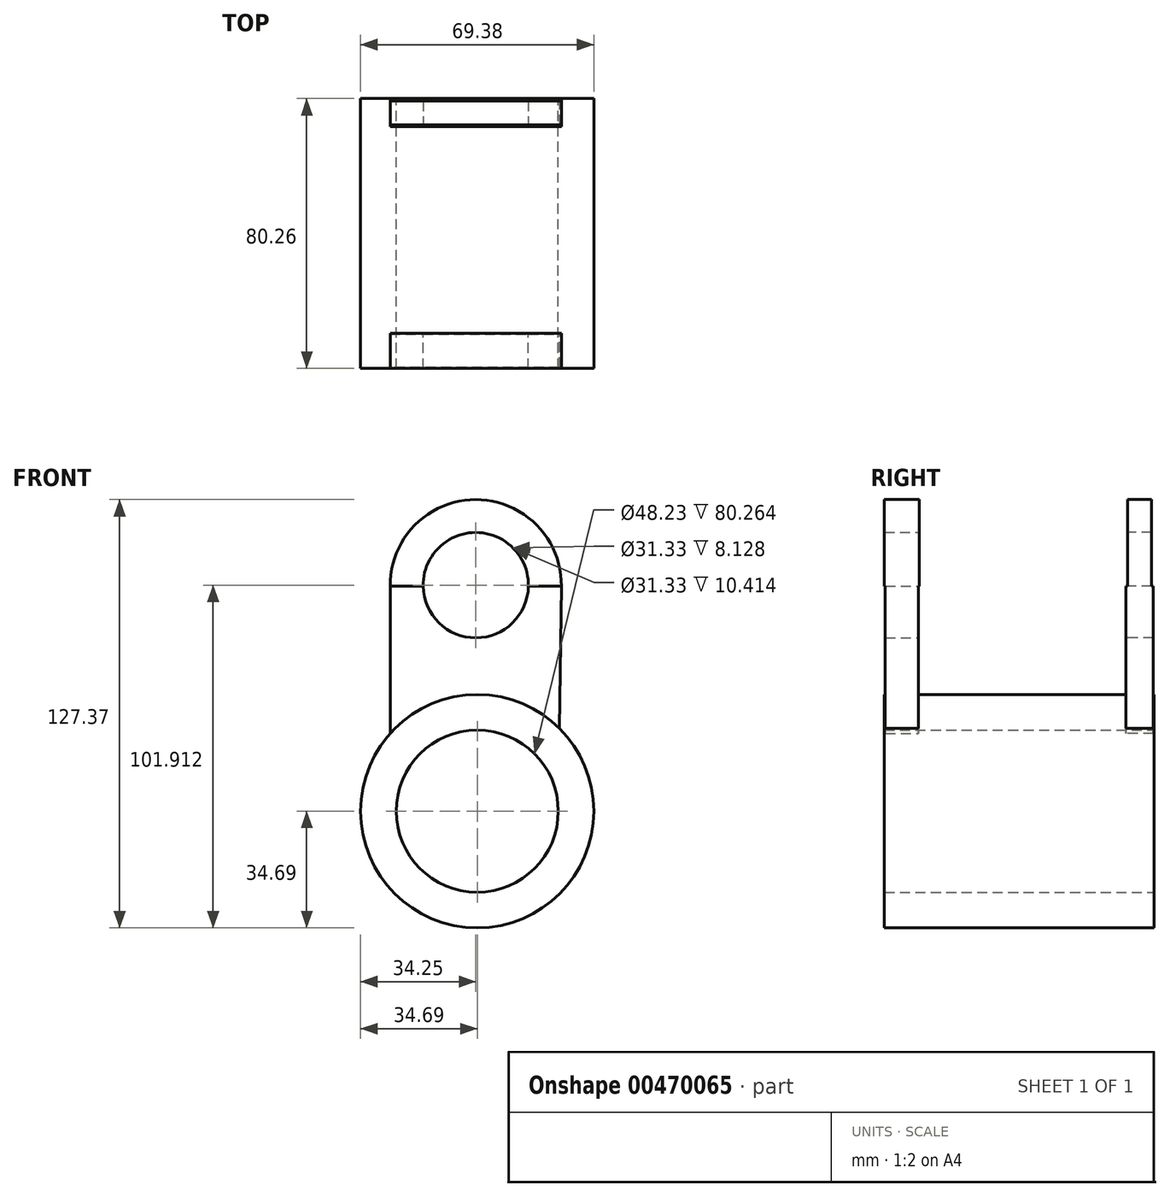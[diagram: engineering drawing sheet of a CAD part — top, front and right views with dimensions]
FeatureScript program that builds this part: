
annotation { "Feature Type Name" : "Feature", "Feature Type Description" : "" }
export const myFeature = defineFeature(function(context is Context, id is Id, definition is map)
    precondition{}
    {
        {
            var Q0;
            Q0=qCreatedBy(makeId("Front.planeOp"),FACE);
            var sketch = newSketch(context, id + "F0", { "sketchPlane" : qUnion([Q0])});
            skCircle(sketch, "E0", {"center": v(0, 0) * mm, "radius": 24.11 * mm});
            skCircle(sketch, "E1", {"center": v(0, 0) * mm, "radius": 34.69 * mm});
            skLineSegment(sketch, "E2", {"start": v(-25.9, 23.08) * mm, "end": v(-25.9, 66.88) * mm});
            skLineSegment(sketch, "E3", {"start": v(-25.9, 66.88) * mm, "end": v(25.02, 66.88) * mm});
            skLineSegment(sketch, "E4", {"start": v(25.02, 66.88) * mm, "end": v(24.45, 24.61) * mm});
            skArc(sketch, "E5", {"start": v(25.02, 66.88) * mm, "mid": v(-0.44, 92.68) * mm, "end": v(-25.9, 66.88) * mm});
            skCircle(sketch, "E6", {"center": v(-0.44, 67.22) * mm, "radius": 15.66 * mm});
            skSolve(sketch);
        }
        {
            var Q0;
            Q0=makeQuery(id+"F0.imprint","IMPRINT",FACE,{"disambiguationData":[TD([[makeQuery(id+"F0.imprint","IMPRINT",EDGE,{"derivedFrom":sQuery(id+"F0.wireOp",EDGE,"E0")}),-1.0]])]});
            extrude(context, id + "F1", {"entities" : qUnion([Q0]), "endBound" : BoundingType.SYMMETRIC, "depth" : 80.26 * mm});
        }
        {
            var Q0;
            {var subQ0=sQuery(id+"F0.wireOp",EDGE,"E2");Q0=makeQuery(id+"F0.imprint","IMPRINT",FACE,{"disambiguationData":[TD([[makeQuery(id+"F0.imprint","IMPRINT",EDGE,{"derivedFrom":subQ0}),-1.0]])]});}
            extrude(context, id + "F2", {"entities" : qUnion([Q0]), "operationType" : NewBodyOperationType.ADD, "oppositeDirection" : true, "depth" : 39.88 * mm, "hasSecondDirection" : true, "secondDirectionOppositeDirection" : true, "secondDirectionDepth" : 31.75 * mm});
        }
        {
            var Q0;
            {var subQ0=sQuery(id+"F0.wireOp",EDGE,"E2");Q0=makeQuery(id+"F0.imprint","IMPRINT",FACE,{"disambiguationData":[TD([[makeQuery(id+"F0.imprint","IMPRINT",EDGE,{"derivedFrom":subQ0}),-1.0]])]});}
            extrude(context, id + "F3", {"entities" : qUnion([Q0]), "operationType" : NewBodyOperationType.ADD, "depth" : 39.88 * mm, "hasSecondDirection" : true, "secondDirectionOppositeDirection" : false, "secondDirectionDepth" : 29.97 * mm});
        }
        {
            var Q0;
            {var subQ0=sQuery(id+"F0.wireOp",EDGE,"E5");Q0=makeQuery(id+"F0.imprint","IMPRINT",FACE,{"disambiguationData":[TD([[makeQuery(id+"F0.imprint","IMPRINT",EDGE,{"derivedFrom":subQ0}),1.0]])]});}
            extrude(context, id + "F4", {"entities" : qUnion([Q0]), "operationType" : NewBodyOperationType.ADD, "depth" : 40.13 * mm, "hasSecondDirection" : true, "secondDirectionOppositeDirection" : false, "secondDirectionDepth" : 29.72 * mm});
        }
        {
            var Q0;
            {var subQ0=sQuery(id+"F0.wireOp",EDGE,"E5");Q0=makeQuery(id+"F0.imprint","IMPRINT",FACE,{"disambiguationData":[TD([[makeQuery(id+"F0.imprint","IMPRINT",EDGE,{"derivedFrom":subQ0}),1.0]])]});}
            extrude(context, id + "F5", {"entities" : qUnion([Q0]), "operationType" : NewBodyOperationType.ADD, "oppositeDirection" : true, "depth" : 39.37 * mm, "hasSecondDirection" : true, "secondDirectionOppositeDirection" : true, "secondDirectionDepth" : 32.26 * mm});
        }
    });
